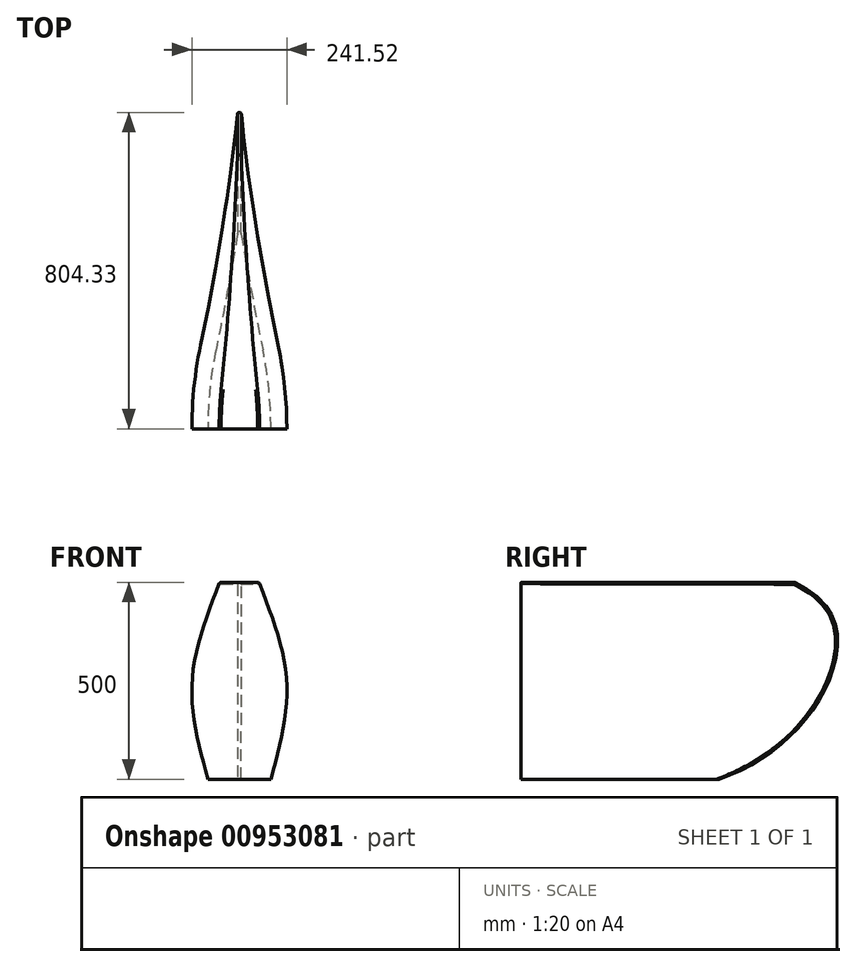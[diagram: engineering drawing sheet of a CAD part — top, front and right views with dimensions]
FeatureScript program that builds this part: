
annotation { "Feature Type Name" : "Feature", "Feature Type Description" : "" }
export const myFeature = defineFeature(function(context is Context, id is Id, definition is map)
    precondition{}
    {
        {
            var Q0;
            Q0=qCreatedBy(makeId("Right.planeOp"),FACE);
            var sketch = newSketch(context, id + "F0", { "sketchPlane" : qUnion([Q0])});
            skLineSegment(sketch, "E0.bottom", {"start": v(-20.36, 500) * mm, "end": v(853.35, 500) * mm, "construction": true});
            skLineSegment(sketch, "E0.top", {"start": v(-20.36, 0) * mm, "end": v(500, 0) * mm, "construction": true});
            skLineSegment(sketch, "E0.left", {"start": v(-20.36, 500) * mm, "end": v(-20.36, 0) * mm});
            skArc(sketch, "E1", {"start": v(500, 0) * mm, "mid": v(761.36, 190.15) * mm, "end": v(853.35, 500) * mm});
            skSolve(sketch);
        }
        {
            var Q0;
            Q0=qCreatedBy(makeId("Top.planeOp"),FACE);
            var Q1;
            Q1=sQuery(id+"F0.wireOp",VERTEX,"E0.bottom.start");
            cPlane(context, id + "F1", {"entities" : qUnion([Q0, Q1]), "cplaneType" : CPlaneType.PLANE_POINT, "offset" : 25 * mm, "width" : 150 * mm, "height" : 150 * mm});
        }
        {
            var Q0;
            Q0=sQuery(id+"F0.wireOp",EDGE,"E0.left");
            cPoint(context, id + "F2", {"entities" : qUnion([Q0]), "parameter" : 0.5});
        }
        {
            var Q0;
            Q0=qCreatedBy(makeId("Top.planeOp"),FACE);
            var Q1;
            Q1 = qCreatedBy(id + "F2" ,VERTEX);
            cPlane(context, id + "F3", {"entities" : qUnion([Q0, Q1]), "cplaneType" : CPlaneType.PLANE_POINT, "offset" : 25 * mm, "width" : 150 * mm, "height" : 150 * mm});
        }
        {
            var Q0;
            Q0=qCreatedBy(makeId("Top.planeOp"),FACE);
            var sketch = newSketch(context, id + "F4", { "sketchPlane" : qUnion([Q0])});
            skLineSegment(sketch, "E2", {"start": v(0, -20.36) * mm, "end": v(80, -20.36) * mm});
            skLineSegment(sketch, "E3", {"start": v(0, -20.36) * mm, "end": v(0, 500) * mm});
            skArc(sketch, "E4", {"start": v(80, -20.36) * mm, "mid": v(74.94, 80.15) * mm, "end": v(59.8, 179.64) * mm});
            skArc(sketch, "E5", {"start": v(59.8, 179.64) * mm, "mid": v(28.55, 339.57) * mm, "end": v(0, 500) * mm});
            skSolve(sketch);
        }
        {
            var Q0;
            Q0=qCreatedBy(id+"F1.planeOp",FACE);
            var sketch = newSketch(context, id + "F5", { "sketchPlane" : qUnion([Q0])});
            skLineSegment(sketch, "E6", {"start": v(0, -20.36) * mm, "end": v(50, -20.36) * mm});
            skLineSegment(sketch, "E7", {"start": v(0, -20.36) * mm, "end": v(0, 853.35) * mm});
            skArc(sketch, "E8", {"start": v(50, -20.36) * mm, "mid": v(48.75, 29.7) * mm, "end": v(44.99, 79.64) * mm});
            skArc(sketch, "E9", {"start": v(44.99, 79.64) * mm, "mid": v(14.35, 466.03) * mm, "end": v(0, 853.35) * mm});
            skSolve(sketch);
        }
        {
            var Q0;
            Q0=qCreatedBy(id+"F3.planeOp",FACE);
            var sketch = newSketch(context, id + "F6", { "sketchPlane" : qUnion([Q0])});
            skLineSegment(sketch, "E10", {"start": v(0, -20.36) * mm, "end": v(120, -20.36) * mm});
            skLineSegment(sketch, "E11", {"start": v(0, -20.36) * mm, "end": v(0, 797.7) * mm});
            skArc(sketch, "E12", {"start": v(120, -20.36) * mm, "mid": v(114.94, 80.15) * mm, "end": v(99.8, 179.64) * mm});
            skArc(sketch, "E13", {"start": v(99.8, 179.64) * mm, "mid": v(43.52, 487.64) * mm, "end": v(0, 797.7) * mm});
            skSolve(sketch);
        }
        {
            var Q0;
            Q0=makeQuery(id+"F4.imprint","IMPRINT",FACE,{"disambiguationData":[TD([[makeQuery(id+"F4.imprint","IMPRINT",EDGE,{"derivedFrom":sQuery(id+"F4.wireOp",EDGE,"E2")}),1.0]])]});
            var Q1;
            Q1=makeQuery(id+"F6.imprint","IMPRINT",FACE,{"disambiguationData":[TD([[makeQuery(id+"F6.imprint","IMPRINT",EDGE,{"derivedFrom":sQuery(id+"F6.wireOp",EDGE,"E10")}),1.0]])]});
            var Q2;
            Q2=makeQuery(id+"F5.imprint","IMPRINT",FACE,{"disambiguationData":[TD([[makeQuery(id+"F5.imprint","IMPRINT",EDGE,{"derivedFrom":sQuery(id+"F5.wireOp",EDGE,"E6")}),1.0]])]});
            var Q3;
            Q3=sQuery(id+"F0.wireOp",EDGE,"E0.left");
            var Q4;
            Q4=sQuery(id+"F0.wireOp",EDGE,"E1");
            var Q5;
            Q5=sQuery(id+"F0.wireOp",EDGE,"E0.left");
            loft(context, id + "F7", {"sheetProfilesArray" : [{ "sheetProfileEntities" : qUnion([Q0]) }, { "sheetProfileEntities" : qUnion([Q1]) }, { "sheetProfileEntities" : qUnion([Q2]) }], "addGuides" : true, "guidesArray" : [{ "guideEntities" : qUnion([Q3]), "guideDerivativeType" : LoftGuideDerivativeType.DEFAULT, "guideDerivativeMagnitude" : 1 }, { "guideEntities" : qUnion([Q4]), "guideDerivativeType" : LoftGuideDerivativeType.DEFAULT, "guideDerivativeMagnitude" : 1 }], "spine" : qUnion([Q5])});
        }
        {
            var Q0;
            Q0=makeQuery(id+"F7.opLoft","SWEPT_BODY",BODY,{"disambiguationData":[OSD([sQuery(id+"F0.wireOp",EDGE,"E0.left"),sQuery(id+"F0.wireOp",EDGE,"E1"),makeQuery(id+"F4.imprint","IMPRINT",FACE,{"disambiguationData":[TD([[makeQuery(id+"F4.imprint","IMPRINT",EDGE,{"derivedFrom":sQuery(id+"F4.wireOp",EDGE,"E2")}),1.0]])]}),makeQuery(id+"F5.imprint","IMPRINT",FACE,{"disambiguationData":[TD([[makeQuery(id+"F5.imprint","IMPRINT",EDGE,{"derivedFrom":sQuery(id+"F5.wireOp",EDGE,"E6")}),1.0]])]}),sQuery(id+"F6.wireOp",EDGE,"E12")])]});
            var Q1;
            Q1=qCreatedBy(makeId("Right.planeOp"),FACE);
            mirror(context, id + "F8", {"operationType" : NewBodyOperationType.ADD, "entities" : qUnion([Q0]), "mirrorPlane" : qUnion([Q1])});
        }
        {
            var Q0;
            {var subQ0=makeQuery(id+"F7.opLoft","SWEPT_EDGE",EDGE,{"disambiguationData":[OSD([sQuery(id+"F0.wireOp",EDGE,"E1"),sQuery(id+"F4.wireOp",EDGE,"E3"),sQuery(id+"F4.wireOp",EDGE,"E5"),sQuery(id+"F5.wireOp",EDGE,"E7"),sQuery(id+"F5.wireOp",EDGE,"E9"),sQuery(id+"F6.wireOp",EDGE,"E11"),sQuery(id+"F6.wireOp",EDGE,"E13")])]});Q0=makeQuery(id+"F8.boolean.opBoolean","MERGE",EDGE,{"derivedFrom":[subQ0,makeQuery(id+"F8.opPattern","COPY",EDGE,{"derivedFrom":subQ0,"instanceName":"1"})]});}
            fillet(context, id + "F9", {"entities" : qUnion([Q0]), "tangentPropagation" : true, "radius" : 5 * mm, "defaultsChanged" : false, "vertexSettings" : [], "allowEdgeOverflow" : false});
        }
        {
            var Q0;
            Q0=makeQuery(id+"F7.opLoft","MID_CAP_EDGE",EDGE,{"disambiguationData":[OSD([sQuery(id+"F5.wireOp",EDGE,"E7"),sQuery(id+"F5.wireOp",EDGE,"E8"),sQuery(id+"F5.wireOp",EDGE,"E9")])],"capPos":2.0});
            fillet(context, id + "F10", {"entities" : qUnion([Q0]), "tangentPropagation" : true, "radius" : 5 * mm, "defaultsChanged" : false, "vertexSettings" : [], "allowEdgeOverflow" : false});
        }
    });
